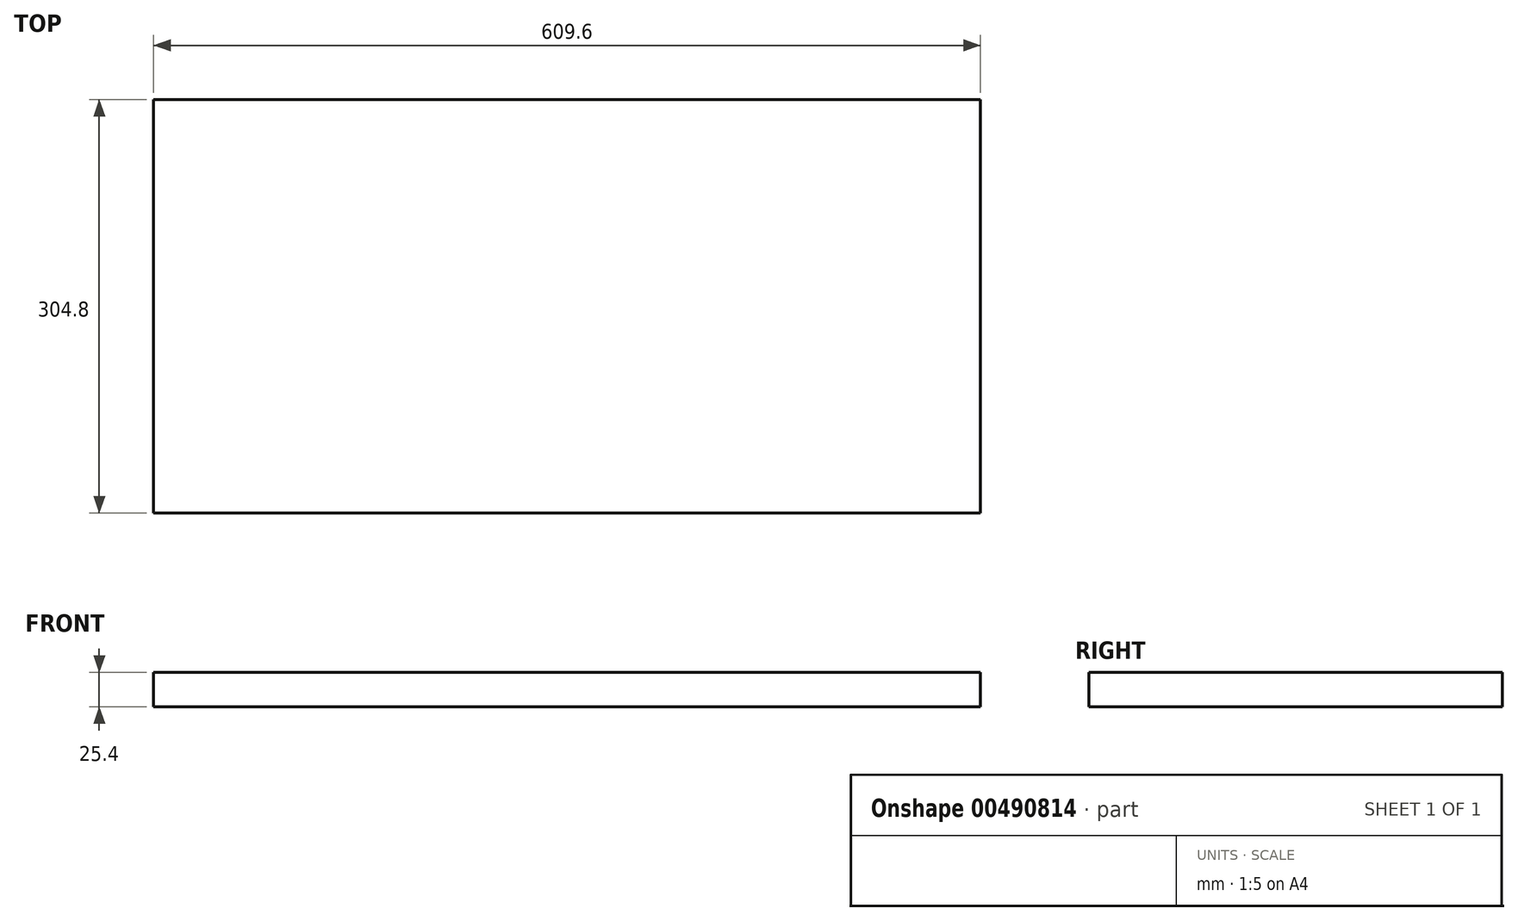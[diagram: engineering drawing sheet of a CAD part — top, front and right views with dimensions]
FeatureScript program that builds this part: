
annotation { "Feature Type Name" : "Feature", "Feature Type Description" : "" }
export const myFeature = defineFeature(function(context is Context, id is Id, definition is map)
    precondition{}
    {
        {
            var Q0;
            Q0=qCreatedBy(makeId("Top.planeOp"),FACE);
            var sketch = newSketch(context, id + "F0", { "sketchPlane" : qUnion([Q0])});
            skLineSegment(sketch, "E0.bottom", {"start": v(-288.78, 138.66) * mm, "end": v(320.82, 138.66) * mm});
            skLineSegment(sketch, "E0.top", {"start": v(-288.78, -166.14) * mm, "end": v(320.82, -166.14) * mm});
            skLineSegment(sketch, "E0.left", {"start": v(-288.78, 138.66) * mm, "end": v(-288.78, -166.14) * mm});
            skLineSegment(sketch, "E0.right", {"start": v(320.82, 138.66) * mm, "end": v(320.82, -166.14) * mm});
            skSolve(sketch);
        }
        {
            var Q0;
            Q0 = qSketchRegion(id + "F0", true);
            extrude(context, id + "F1", {"entities" : qUnion([Q0]), "depth" : 25.4 * mm});
        }
    });
